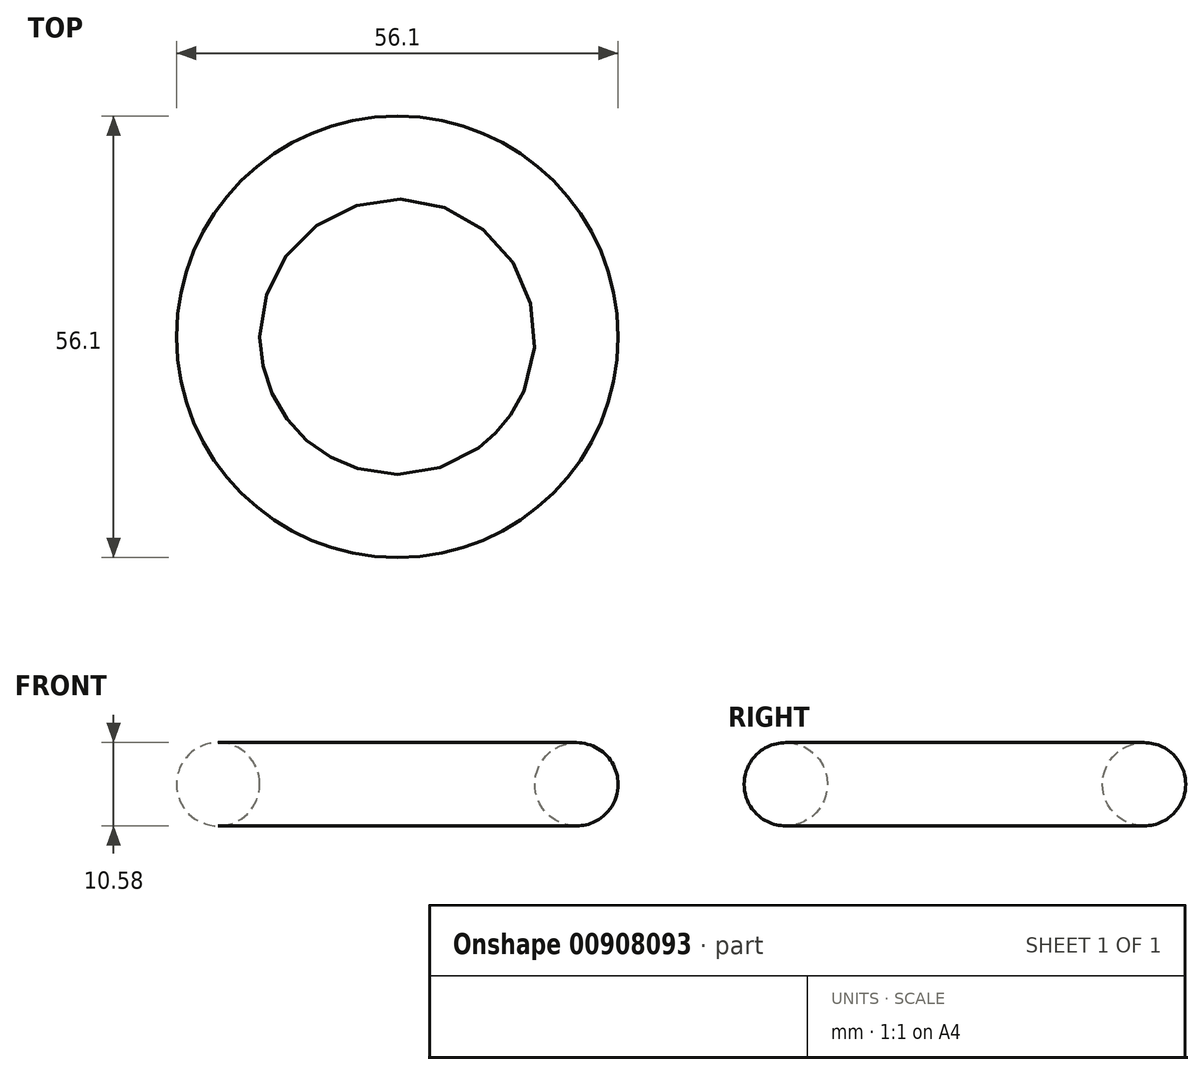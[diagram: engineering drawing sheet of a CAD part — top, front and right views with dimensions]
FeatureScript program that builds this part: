
annotation { "Feature Type Name" : "Feature", "Feature Type Description" : "" }
export const myFeature = defineFeature(function(context is Context, id is Id, definition is map)
    precondition{}
    {
        {
            var Q0;
            Q0=qCreatedBy(makeId("Top.planeOp"),FACE);
            var sketch = newSketch(context, id + "F0", { "sketchPlane" : qUnion([Q0])});
            skCircle(sketch, "E0", {"center": v(0, 0) * mm, "radius": 22.85 * mm});
            skSolve(sketch);
        }
        {
            var Q0;
            Q0=qCreatedBy(makeId("Front.planeOp"),FACE);
            var sketch = newSketch(context, id + "F1", { "sketchPlane" : qUnion([Q0])});
            skCircle(sketch, "E1", {"center": v(-22.76, 0) * mm, "radius": 5.29 * mm});
            skSolve(sketch);
        }
        {
            var Q0;
            Q0=makeQuery(id+"F1.imprint","IMPRINT",FACE,{"disambiguationData":[TD([[makeQuery(id+"F1.imprint","IMPRINT",EDGE,{"derivedFrom":sQuery(id+"F1.wireOp",EDGE,"E1")}),1.0]])]});
            var Q1;
            Q1=sQuery(id+"F0.wireOp",EDGE,"E0");
            revolve(context, id + "F2", {"surfaceOperationType" : NewSurfaceOperationType.NEW, "entities" : qUnion([Q0]), "axis" : qUnion([Q1]), "revolveType" : RevolveType.FULL});
        }
    });
